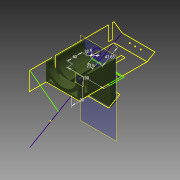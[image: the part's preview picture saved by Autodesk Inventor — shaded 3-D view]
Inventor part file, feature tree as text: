
AUTODESK INVENTOR PART (.ipt)
format: ipt  version: 2013 (Build 170138000, 138)  size: 433,664 bytes
history: native  units: mm
features: sketch x26, extrude x20, other x3, hole x1
ambient origin geometry x8: Origin, YZ Plane, XZ Plane, XY Plane, X Axis, Y Axis, Z Axis, Center Point
feature tree (50):
  other  "ソリッド1"
  extrude  "押し出し1"  Depth=90.0mm
  extrude  "押し出し2"  Depth=50.0mm
  extrude  "押し出し3"  Depth=5.0mm
  extrude  "押し出し4"  Depth=85.0mm
  extrude  "押し出し6"  Depth=5.0mm
  sketch  "スケッチ9"
  hole  "穴1"  [1 undecoded]
  extrude  "押し出し12"  Depth=10.0mm
  sketch  "スケッチ19"
  sketch  "スケッチ20"
  other  "作業平面5"
  extrude  "押し出し13"  Depth=90.0mm
  other  "作業平面6"
  extrude  "押し出し14"  Depth=230.0mm TaperAngle=0.0deg
  extrude  "押し出し15"  Depth=225.0mm TaperAngle=0.0deg
  sketch  "スケッチ24"
  sketch  "スケッチ25"
  extrude  "押し出し16"  Depth=5.0mm TaperAngle=0.0deg
  sketch  "スケッチ27"
  extrude  "押し出し17"  Depth=60.0mm
  extrude  "押し出し18"  Depth=10.0mm
  extrude  "押し出し19"  Depth=140.0mm
  extrude  "押し出し20"  Depth=10.0mm
  extrude  "押し出し21"  Depth=40.0mm
  extrude  "押し出し22"  Depth=90.0mm TaperAngle=0.0deg
  extrude  "押し出し23"  Depth=48.0mm
  extrude  "押し出し24"  TaperAngle=120.0deg  [1 undecoded]
  extrude  "押し出し25"  TaperAngle=30.0deg  [1 undecoded]
  extrude  "押し出し26"  Depth=90.0mm TaperAngle=0.0deg
  sketch  "スケッチ1"
  sketch  "スケッチ2"
  sketch  "スケッチ3"
  sketch  "スケッチ4"
  sketch  "スケッチ6"
  sketch  "スケッチ11"
  sketch  "スケッチ18"
  sketch  "スケッチ21"
  sketch  "スケッチ22"
  sketch  "スケッチ23"
  sketch  "スケッチ26"
  sketch  "スケッチ28"
  sketch  "スケッチ29"
  sketch  "スケッチ30"
  sketch  "スケッチ31"
  sketch  "スケッチ32"
  sketch  "スケッチ33"
  sketch  "スケッチ34"
  sketch  "スケッチ35"
  sketch  "スケッチ36"
note: 3 required parameter values undecoded (feature->parameter linkage not recoverable at this tier; creation-order binding heuristic only, values carry confidence <= 0.55)
